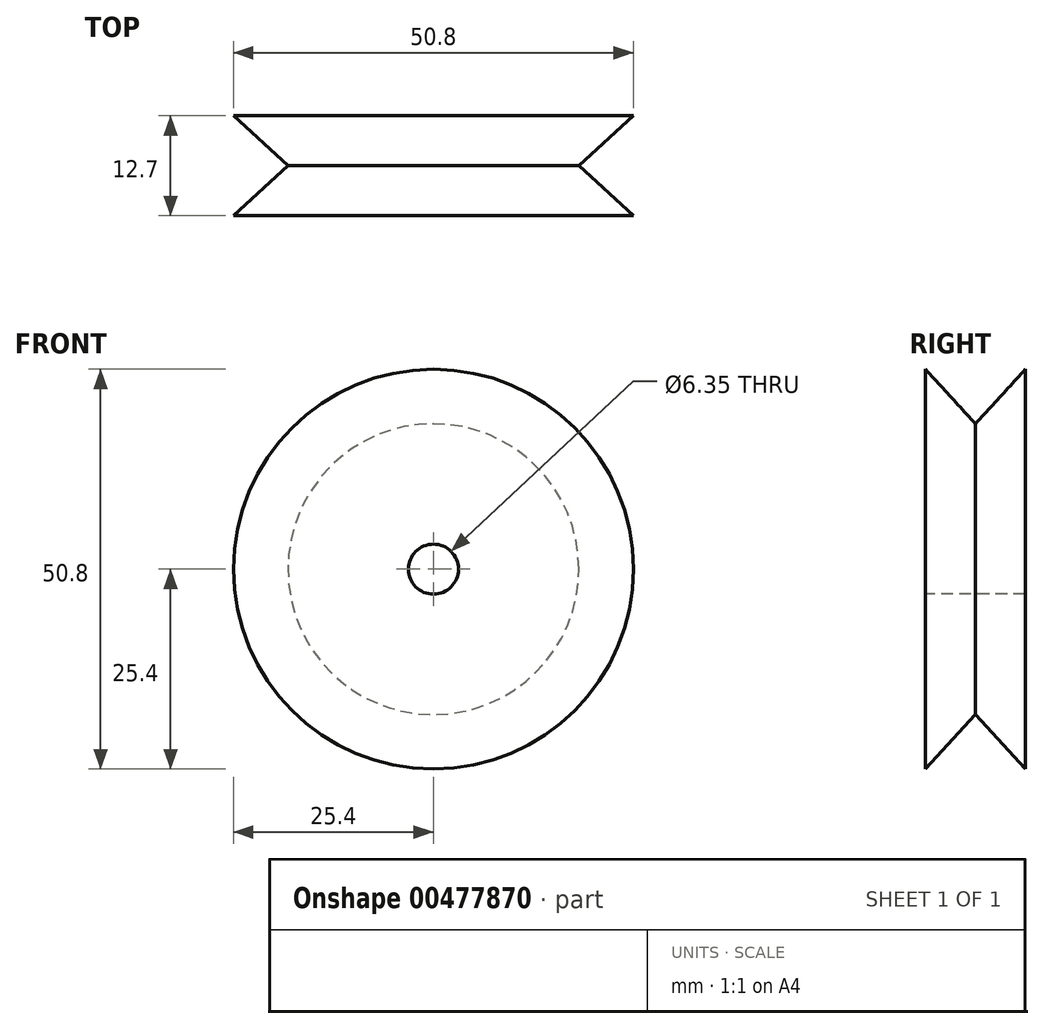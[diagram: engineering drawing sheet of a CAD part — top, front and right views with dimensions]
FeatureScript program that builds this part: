
annotation { "Feature Type Name" : "Feature", "Feature Type Description" : "" }
export const myFeature = defineFeature(function(context is Context, id is Id, definition is map)
    precondition{}
    {
        {
            var Q0;
            Q0=qCreatedBy(makeId("Right.planeOp"),FACE);
            var sketch = newSketch(context, id + "F0", { "sketchPlane" : qUnion([Q0])});
            skLineSegment(sketch, "E0", {"start": v(0, 0) * mm, "end": v(0, 25.4) * mm});
            skLineSegment(sketch, "E1", {"start": v(0, 25.4) * mm, "end": v(6.35, 18.47) * mm});
            skLineSegment(sketch, "E2", {"start": v(6.35, 18.47) * mm, "end": v(12.7, 25.4) * mm});
            skLineSegment(sketch, "E3", {"start": v(12.7, 25.4) * mm, "end": v(12.7, 0) * mm});
            skLineSegment(sketch, "E4", {"start": v(12.7, 0) * mm, "end": v(0, 0) * mm});
            skSolve(sketch);
        }
        {
            var Q0;
            Q0=makeQuery(id+"F0.imprint","IMPRINT",FACE,{"disambiguationData":[TD([[makeQuery(id+"F0.imprint","IMPRINT",EDGE,{"derivedFrom":sQuery(id+"F0.wireOp",EDGE,"E0")}),-1.0]])]});
            var Q1;
            Q1=sQuery(id+"F0.wireOp",EDGE,"E4");
            revolve(context, id + "F1", {"entities" : qUnion([Q0]), "axis" : qUnion([Q1]), "revolveType" : RevolveType.FULL});
        }
        {
            var Q0;
            Q0=makeQuery(id+"F1.opRevolve","SWEPT_FACE",FACE,{"disambiguationData":[OSD([sQuery(id+"F0.wireOp",EDGE,"E0")])]});
            var sketch = newSketch(context, id + "F2", { "sketchPlane" : qUnion([Q0])});
            skPoint(sketch, "E5", {"position": v(0, 0) * mm});
            skSolve(sketch);
        }
        {
            var Q0;
            Q0=sQuery(id+"F2.wireOp",VERTEX,"E5");
            var Q1;
            Q1=makeQuery(id+"F1.opRevolve","SWEPT_BODY",BODY,{"disambiguationData":[OSD([sQuery(id+"F0.wireOp",EDGE,"E0"),sQuery(id+"F0.wireOp",EDGE,"E1"),sQuery(id+"F0.wireOp",EDGE,"E2"),sQuery(id+"F0.wireOp",EDGE,"E3"),sQuery(id+"F0.wireOp",EDGE,"E4")])]});
            hole(context, id + "F3", {"style" : HoleStyle.SIMPLE, "endStyle" : HoleEndStyle.THROUGH, "holeDiameter" : 6.35 * mm, "isTappedThrough" : true, "tappedDepth" : 12.7 * mm, "tapClearance" : 3, "locations" : qUnion([Q0]), "scope" : qUnion([Q1])});
        }
    });
